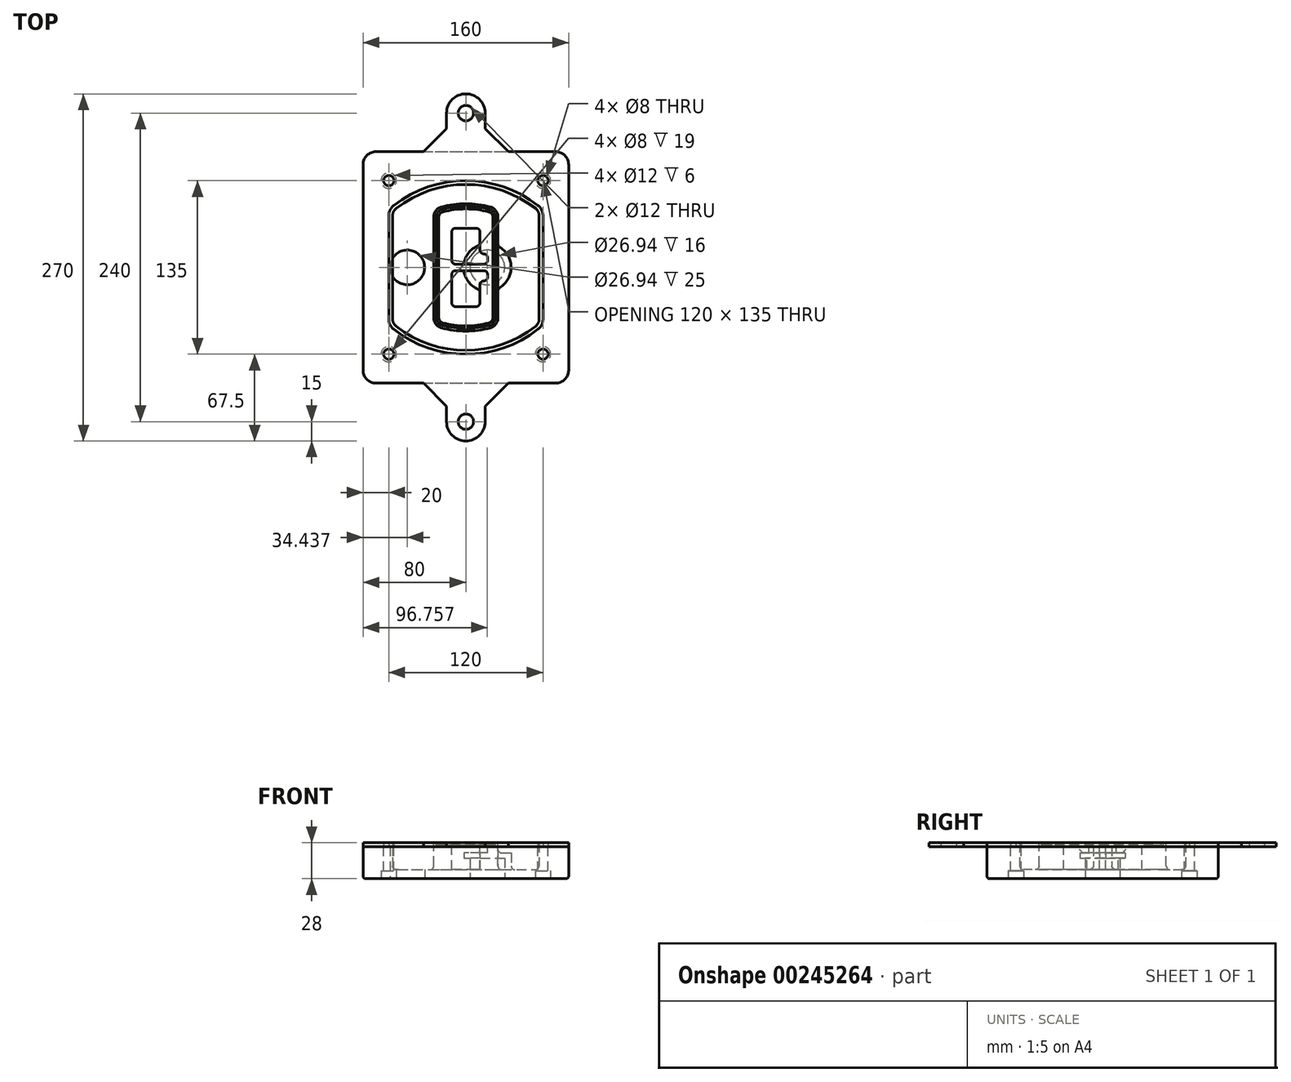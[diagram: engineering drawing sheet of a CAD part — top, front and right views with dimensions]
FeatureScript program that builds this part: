
annotation { "Feature Type Name" : "Feature", "Feature Type Description" : "" }
export const myFeature = defineFeature(function(context is Context, id is Id, definition is map)
    precondition{}
    {
        {
            var Q0;
            Q0=qCreatedBy(makeId("Top.planeOp"),FACE);
            var sketch = newSketch(context, id + "F0", { "sketchPlane" : qUnion([Q0])});
            skPoint(sketch, "E0.rect.middle", {"position": v(0, 0) * mm});
            skLineSegment(sketch, "E1.bottom", {"start": v(-70, -90) * mm, "end": v(70, -90) * mm});
            skLineSegment(sketch, "E1.top", {"start": v(-70, 90) * mm, "end": v(70, 90) * mm});
            skLineSegment(sketch, "E1.left", {"start": v(-80, -80) * mm, "end": v(-80, 80) * mm});
            skLineSegment(sketch, "E1.right", {"start": v(80, -80) * mm, "end": v(80, 80) * mm});
            skLineSegment(sketch, "E2", {"start": v(-80, 90) * mm, "end": v(80, -90) * mm, "construction": true});
            skLineSegment(sketch, "E3", {"start": v(80, 90) * mm, "end": v(-80, -90) * mm, "construction": true});
            skCircle(sketch, "E4", {"center": v(-60, 67.5) * mm, "radius": 4 * mm});
            skCircle(sketch, "E5", {"center": v(60, 67.5) * mm, "radius": 4 * mm});
            skCircle(sketch, "E6", {"center": v(60, -67.5) * mm, "radius": 4 * mm});
            skCircle(sketch, "E7", {"center": v(-60, -67.5) * mm, "radius": 4 * mm});
            skLineSegment(sketch, "E8", {"start": v(-60, 67.5) * mm, "end": v(60, 67.5) * mm, "construction": true});
            skLineSegment(sketch, "E9", {"start": v(60, 67.5) * mm, "end": v(60, -67.5) * mm, "construction": true});
            skLineSegment(sketch, "E10", {"start": v(60, -67.5) * mm, "end": v(-60, -67.5) * mm, "construction": true});
            skLineSegment(sketch, "E11", {"start": v(-60, -67.5) * mm, "end": v(-60, 67.5) * mm, "construction": true});
            skLineSegment(sketch, "E12", {"start": v(-60, 40.3) * mm, "end": v(-60, -40.3) * mm});
            skLineSegment(sketch, "E13", {"start": v(60, 40.3) * mm, "end": v(60, -40.3) * mm});
            skArc(sketch, "E14", {"start": v(56.15, 48.18) * mm, "mid": v(0, 67.5) * mm, "end": v(-56.15, 48.18) * mm});
            skArc(sketch, "E15", {"start": v(-56.15, -48.18) * mm, "mid": v(0, -67.5) * mm, "end": v(56.15, -48.18) * mm});
            skLineSegment(sketch, "E16", {"start": v(-60, 0) * mm, "end": v(60, 0) * mm, "construction": true});
            skPoint(sketch, "E17.visualSharp", {"position": v(-60, -45) * mm});
            skArc(sketch, "E17.filletArc", {"start": v(-60, -40.3) * mm, "mid": v(-58.99, -44.68) * mm, "end": v(-56.15, -48.18) * mm});
            skPoint(sketch, "E18.visualSharp", {"position": v(-60, 45) * mm});
            skArc(sketch, "E18.filletArc", {"start": v(-56.15, 48.18) * mm, "mid": v(-58.99, 44.68) * mm, "end": v(-60, 40.3) * mm});
            skPoint(sketch, "E19.visualSharp", {"position": v(60, 45) * mm});
            skArc(sketch, "E19.filletArc", {"start": v(60, 40.3) * mm, "mid": v(58.99, 44.68) * mm, "end": v(56.15, 48.18) * mm});
            skPoint(sketch, "E20.visualSharp", {"position": v(60, -45) * mm});
            skArc(sketch, "E20.filletArc", {"start": v(56.15, -48.18) * mm, "mid": v(58.99, -44.68) * mm, "end": v(60, -40.3) * mm});
            skPoint(sketch, "E21.visualSharp", {"position": v(-80, 90) * mm});
            skArc(sketch, "E21.filletArc", {"start": v(-70, 90) * mm, "mid": v(-77.07, 87.07) * mm, "end": v(-80, 80) * mm});
            skPoint(sketch, "E22.visualSharp", {"position": v(80, 90) * mm});
            skArc(sketch, "E22.filletArc", {"start": v(80, 80) * mm, "mid": v(77.07, 87.07) * mm, "end": v(70, 90) * mm});
            skPoint(sketch, "E23.visualSharp", {"position": v(80, -90) * mm});
            skArc(sketch, "E23.filletArc", {"start": v(70, -90) * mm, "mid": v(77.07, -87.07) * mm, "end": v(80, -80) * mm});
            skPoint(sketch, "E24.visualSharp", {"position": v(-80, -90) * mm});
            skArc(sketch, "E24.filletArc", {"start": v(-80, -80) * mm, "mid": v(-77.07, -87.07) * mm, "end": v(-70, -90) * mm});
            skArc(sketch, "E25.0", {"start": v(57, 40.3) * mm, "mid": v(56.3, 43.36) * mm, "end": v(54.3, 45.81) * mm});
            skLineSegment(sketch, "E25.1", {"start": v(57, 40.3) * mm, "end": v(57, -40.3) * mm});
            skArc(sketch, "E25.2", {"start": v(54.3, -45.81) * mm, "mid": v(56.3, -43.36) * mm, "end": v(57, -40.3) * mm});
            skArc(sketch, "E25.3", {"start": v(-54.3, -45.81) * mm, "mid": v(0, -64.5) * mm, "end": v(54.3, -45.81) * mm});
            skArc(sketch, "E25.4", {"start": v(-57, -40.3) * mm, "mid": v(-56.3, -43.36) * mm, "end": v(-54.3, -45.81) * mm});
            skArc(sketch, "E25.5", {"start": v(54.3, 45.81) * mm, "mid": v(0, 64.5) * mm, "end": v(-54.3, 45.81) * mm});
            skLineSegment(sketch, "E25.6", {"start": v(-57, 40.3) * mm, "end": v(-57, -40.3) * mm});
            skArc(sketch, "E25.7", {"start": v(-54.3, 45.81) * mm, "mid": v(-56.3, 43.36) * mm, "end": v(-57, 40.3) * mm});
            skArc(sketch, "E26.0", {"start": v(-58.62, 51.33) * mm, "mid": v(-62.58, 46.43) * mm, "end": v(-64, 40.3) * mm});
            skArc(sketch, "E26.1", {"start": v(58.62, 51.33) * mm, "mid": v(0, 71.5) * mm, "end": v(-58.62, 51.33) * mm});
            skArc(sketch, "E26.2", {"start": v(64, 40.3) * mm, "mid": v(62.58, 46.43) * mm, "end": v(58.62, 51.33) * mm});
            skLineSegment(sketch, "E26.3", {"start": v(64, 40.3) * mm, "end": v(64, -40.3) * mm});
            skArc(sketch, "E26.4", {"start": v(58.62, -51.33) * mm, "mid": v(62.58, -46.43) * mm, "end": v(64, -40.3) * mm});
            skLineSegment(sketch, "E26.5", {"start": v(-64, 40.3) * mm, "end": v(-64, -40.3) * mm});
            skArc(sketch, "E26.6", {"start": v(-58.62, -51.33) * mm, "mid": v(0, -71.5) * mm, "end": v(58.62, -51.33) * mm});
            skArc(sketch, "E26.7", {"start": v(-64, -40.3) * mm, "mid": v(-62.58, -46.43) * mm, "end": v(-58.62, -51.33) * mm});
            skSolve(sketch);
        }
        {
            var Q0;
            Q0=makeQuery(id+"F0.imprint","IMPRINT",FACE,{"disambiguationData":[TD([[makeQuery(id+"F0.imprint","IMPRINT",EDGE,{"derivedFrom":sQuery(id+"F0.wireOp",EDGE,"E1.bottom")}),1.0]])]});
            var Q1;
            Q1=makeQuery(id+"F0.imprint","IMPRINT",FACE,{"disambiguationData":[TD([[makeQuery(id+"F0.imprint","IMPRINT",EDGE,{"derivedFrom":sQuery(id+"F0.wireOp",EDGE,"E12")}),1.0]])]});
            var Q2;
            Q2=makeQuery(id+"F0.imprint","IMPRINT",FACE,{"disambiguationData":[TD([[makeQuery(id+"F0.imprint","IMPRINT",EDGE,{"derivedFrom":sQuery(id+"F0.wireOp",EDGE,"E25.0")}),1.0]])]});
            var Q3;
            Q3=makeQuery(id+"F0.imprint","IMPRINT",FACE,{"disambiguationData":[TD([[makeQuery(id+"F0.imprint","IMPRINT",EDGE,{"derivedFrom":sQuery(id+"F0.wireOp",EDGE,"E12")}),-1.0]])]});
            extrude(context, id + "F1", {"entities" : qUnion([Q0, Q1, Q2, Q3]), "oppositeDirection" : true, "depth" : 25 * mm});
        }
        {
            var Q0;
            Q0=makeQuery(id+"F0.imprint","IMPRINT",FACE,{"disambiguationData":[TD([[makeQuery(id+"F0.imprint","IMPRINT",EDGE,{"derivedFrom":sQuery(id+"F0.wireOp",EDGE,"E12")}),1.0]])]});
            extrude(context, id + "F2", {"entities" : qUnion([Q0]), "operationType" : NewBodyOperationType.ADD, "depth" : 3 * mm});
        }
        {
            var Q0;
            Q0=makeQuery(id+"F0.imprint","IMPRINT",FACE,{"disambiguationData":[TD([[makeQuery(id+"F0.imprint","IMPRINT",EDGE,{"derivedFrom":sQuery(id+"F0.wireOp",EDGE,"E25.0")}),1.0]])]});
            extrude(context, id + "F3", {"entities" : qUnion([Q0]), "operationType" : NewBodyOperationType.REMOVE, "oppositeDirection" : true, "depth" : 18 * mm});
        }
        {
            var Q0;
            Q0=makeQuery(id+"F2.opExtrude","CAP_FACE",FACE,{"disambiguationData":[OSD([sQuery(id+"F0.wireOp",EDGE,"E12"),sQuery(id+"F0.wireOp",EDGE,"E13"),sQuery(id+"F0.wireOp",EDGE,"E14"),sQuery(id+"F0.wireOp",EDGE,"E15"),sQuery(id+"F0.wireOp",EDGE,"E17.filletArc"),sQuery(id+"F0.wireOp",EDGE,"E18.filletArc"),sQuery(id+"F0.wireOp",EDGE,"E19.filletArc"),sQuery(id+"F0.wireOp",EDGE,"E20.filletArc"),sQuery(id+"F0.wireOp",EDGE,"E25.0"),sQuery(id+"F0.wireOp",EDGE,"E25.1"),sQuery(id+"F0.wireOp",EDGE,"E25.2"),sQuery(id+"F0.wireOp",EDGE,"E25.3"),sQuery(id+"F0.wireOp",EDGE,"E25.4"),sQuery(id+"F0.wireOp",EDGE,"E25.5"),sQuery(id+"F0.wireOp",EDGE,"E25.6"),sQuery(id+"F0.wireOp",EDGE,"E25.7")])],"isStart":false});
            var sketch = newSketch(context, id + "F4", { "sketchPlane" : qUnion([Q0])});
            skArc(sketch, "E27.0", {"start": v(-19.08, -46.97) * mm, "mid": v(0, -49.5) * mm, "end": v(19.08, -46.97) * mm});
            skArc(sketch, "E28.0", {"start": v(19.08, 46.97) * mm, "mid": v(0, 49.5) * mm, "end": v(-19.08, 46.97) * mm});
            skLineSegment(sketch, "E29", {"start": v(-25, 39.25) * mm, "end": v(-25, -39.25) * mm});
            skLineSegment(sketch, "E30", {"start": v(25, 39.25) * mm, "end": v(25, -39.25) * mm});
            skLineSegment(sketch, "E31", {"start": v(-25, 45.1) * mm, "end": v(25, 45.1) * mm, "construction": true});
            skLineSegment(sketch, "E32", {"start": v(-25, -45.1) * mm, "end": v(25, -45.1) * mm, "construction": true});
            skPoint(sketch, "E33.visualSharp", {"position": v(-25, 45.1) * mm});
            skArc(sketch, "E33.filletArc", {"start": v(-19.08, 46.97) * mm, "mid": v(-23.35, 44.11) * mm, "end": v(-25, 39.25) * mm});
            skPoint(sketch, "E34.visualSharp", {"position": v(25, 45.1) * mm});
            skArc(sketch, "E34.filletArc", {"start": v(25, 39.25) * mm, "mid": v(23.35, 44.11) * mm, "end": v(19.08, 46.97) * mm});
            skPoint(sketch, "E35.visualSharp", {"position": v(25, -45.1) * mm});
            skArc(sketch, "E35.filletArc", {"start": v(19.08, -46.97) * mm, "mid": v(23.35, -44.11) * mm, "end": v(25, -39.25) * mm});
            skPoint(sketch, "E36.visualSharp", {"position": v(-25, -45.1) * mm});
            skArc(sketch, "E36.filletArc", {"start": v(-25, -39.25) * mm, "mid": v(-23.35, -44.11) * mm, "end": v(-19.08, -46.97) * mm});
            skArc(sketch, "E37.0", {"start": v(54.3, 45.81) * mm, "mid": v(0, 64.5) * mm, "end": v(-54.3, 45.81) * mm});
            skArc(sketch, "E37.1", {"start": v(-54.3, 45.81) * mm, "mid": v(-56.3, 43.36) * mm, "end": v(-57, 40.3) * mm});
            skLineSegment(sketch, "E37.2", {"start": v(-57, 40.3) * mm, "end": v(-57, -40.3) * mm});
            skArc(sketch, "E37.3", {"start": v(-57, -40.3) * mm, "mid": v(-56.3, -43.36) * mm, "end": v(-54.3, -45.81) * mm});
            skArc(sketch, "E37.4", {"start": v(-54.3, -45.81) * mm, "mid": v(0, -64.5) * mm, "end": v(54.3, -45.81) * mm});
            skArc(sketch, "E37.5", {"start": v(54.3, -45.81) * mm, "mid": v(56.3, -43.36) * mm, "end": v(57, -40.3) * mm});
            skLineSegment(sketch, "E37.6", {"start": v(57, 40.3) * mm, "end": v(57, -40.3) * mm});
            skArc(sketch, "E37.7", {"start": v(57, 40.3) * mm, "mid": v(56.3, 43.36) * mm, "end": v(54.3, 45.81) * mm});
            skLineSegment(sketch, "E38.0", {"start": v(23, 39.25) * mm, "end": v(23, -39.25) * mm});
            skArc(sketch, "E38.1", {"start": v(18.56, -45.04) * mm, "mid": v(21.76, -42.9) * mm, "end": v(23, -39.25) * mm});
            skArc(sketch, "E38.2", {"start": v(-18.56, -45.04) * mm, "mid": v(0, -47.5) * mm, "end": v(18.56, -45.04) * mm});
            skArc(sketch, "E38.3", {"start": v(-23, -39.25) * mm, "mid": v(-21.76, -42.9) * mm, "end": v(-18.56, -45.04) * mm});
            skLineSegment(sketch, "E38.4", {"start": v(-23, 39.25) * mm, "end": v(-23, -39.25) * mm});
            skArc(sketch, "E38.5", {"start": v(23, 39.25) * mm, "mid": v(21.76, 42.9) * mm, "end": v(18.56, 45.04) * mm});
            skArc(sketch, "E38.6", {"start": v(-18.56, 45.04) * mm, "mid": v(-21.76, 42.9) * mm, "end": v(-23, 39.25) * mm});
            skArc(sketch, "E38.7", {"start": v(18.56, 45.04) * mm, "mid": v(0, 47.5) * mm, "end": v(-18.56, 45.04) * mm});
            skArc(sketch, "E39.0", {"start": v(21, 39.25) * mm, "mid": v(20.18, 41.68) * mm, "end": v(18.04, 43.1) * mm});
            skLineSegment(sketch, "E39.1", {"start": v(21, 39.25) * mm, "end": v(21, -39.25) * mm});
            skArc(sketch, "E39.2", {"start": v(18.04, -43.1) * mm, "mid": v(20.18, -41.68) * mm, "end": v(21, -39.25) * mm});
            skArc(sketch, "E39.3", {"start": v(-18.04, -43.1) * mm, "mid": v(0, -45.5) * mm, "end": v(18.04, -43.1) * mm});
            skArc(sketch, "E39.4", {"start": v(-21, -39.25) * mm, "mid": v(-20.18, -41.68) * mm, "end": v(-18.04, -43.1) * mm});
            skArc(sketch, "E39.5", {"start": v(18.04, 43.1) * mm, "mid": v(0, 45.5) * mm, "end": v(-18.04, 43.1) * mm});
            skLineSegment(sketch, "E39.6", {"start": v(-21, 39.25) * mm, "end": v(-21, -39.25) * mm});
            skArc(sketch, "E39.7", {"start": v(-18.04, 43.1) * mm, "mid": v(-20.18, 41.68) * mm, "end": v(-21, 39.25) * mm});
            skLineSegment(sketch, "E40", {"start": v(-25, 0) * mm, "end": v(25, 0) * mm, "construction": true});
            skLineSegment(sketch, "E41", {"start": v(-11, 5.5) * mm, "end": v(-11, 27.5) * mm});
            skLineSegment(sketch, "E42", {"start": v(-8, 30.5) * mm, "end": v(8, 30.5) * mm});
            skLineSegment(sketch, "E43", {"start": v(11, 27.5) * mm, "end": v(11, 13.5) * mm});
            skLineSegment(sketch, "E44", {"start": v(14, 10.5) * mm, "end": v(14, 10.5) * mm});
            skLineSegment(sketch, "E45", {"start": v(17, 7.5) * mm, "end": v(17, 5.5) * mm});
            skLineSegment(sketch, "E46", {"start": v(14, 2.5) * mm, "end": v(-8, 2.5) * mm});
            skPoint(sketch, "E47.visualSharp", {"position": v(-11, 30.5) * mm});
            skArc(sketch, "E47.filletArc", {"start": v(-8, 30.5) * mm, "mid": v(-10.12, 29.62) * mm, "end": v(-11, 27.5) * mm});
            skPoint(sketch, "E48.visualSharp", {"position": v(11, 30.5) * mm});
            skArc(sketch, "E48.filletArc", {"start": v(11, 27.5) * mm, "mid": v(10.12, 29.62) * mm, "end": v(8, 30.5) * mm});
            skPoint(sketch, "E49.visualSharp", {"position": v(11, 10.5) * mm});
            skArc(sketch, "E49.filletArc", {"start": v(11, 13.5) * mm, "mid": v(11.88, 11.38) * mm, "end": v(14, 10.5) * mm});
            skPoint(sketch, "E50.visualSharp", {"position": v(17, 10.5) * mm});
            skArc(sketch, "E50.filletArc", {"start": v(17, 7.5) * mm, "mid": v(16.12, 9.62) * mm, "end": v(14, 10.5) * mm});
            skPoint(sketch, "E51.visualSharp", {"position": v(17, 2.5) * mm});
            skArc(sketch, "E51.filletArc", {"start": v(14, 2.5) * mm, "mid": v(16.12, 3.38) * mm, "end": v(17, 5.5) * mm});
            skPoint(sketch, "E52.visualSharp", {"position": v(-11, 2.5) * mm});
            skArc(sketch, "E52.filletArc", {"start": v(-11, 5.5) * mm, "mid": v(-10.12, 3.38) * mm, "end": v(-8, 2.5) * mm});
            skLineSegment(sketch, "E53.0.MirrorCS", {"start": v(14, -2.5) * mm, "end": v(-8, -2.5) * mm});
            skArc(sketch, "E54.0.MirrorCS", {"start": v(-11, -5.5) * mm, "mid": v(-10.12, -3.38) * mm, "end": v(-8, -2.5) * mm});
            skLineSegment(sketch, "E55.0.MirrorCS", {"start": v(-11, -5.5) * mm, "end": v(-11, -27.5) * mm});
            skArc(sketch, "E56.0.MirrorCS", {"start": v(-8, -30.5) * mm, "mid": v(-10.12, -29.62) * mm, "end": v(-11, -27.5) * mm});
            skLineSegment(sketch, "E57.0.MirrorCS", {"start": v(-8, -30.5) * mm, "end": v(8, -30.5) * mm});
            skArc(sketch, "E58.0.MirrorCS", {"start": v(11, -27.5) * mm, "mid": v(10.12, -29.62) * mm, "end": v(8, -30.5) * mm});
            skLineSegment(sketch, "E59.0.MirrorCS", {"start": v(11, -27.5) * mm, "end": v(11, -13.5) * mm});
            skArc(sketch, "E60.0.MirrorCS", {"start": v(11, -13.5) * mm, "mid": v(11.88, -11.38) * mm, "end": v(14, -10.5) * mm});
            skArc(sketch, "E61.0.MirrorCS", {"start": v(17, -7.5) * mm, "mid": v(16.12, -9.62) * mm, "end": v(14, -10.5) * mm});
            skLineSegment(sketch, "E62.0.MirrorCS", {"start": v(17, -7.5) * mm, "end": v(17, -5.5) * mm});
            skArc(sketch, "E63.0.MirrorCS", {"start": v(14, -2.5) * mm, "mid": v(16.12, -3.38) * mm, "end": v(17, -5.5) * mm});
            skSolve(sketch);
        }
        {
            var Q0;
            Q0=makeQuery(id+"F4.imprint","IMPRINT",FACE,{"disambiguationData":[TD([[makeQuery(id+"F4.imprint","IMPRINT",EDGE,{"derivedFrom":sQuery(id+"F4.wireOp",EDGE,"E27.0")}),1.0]])]});
            var Q1;
            Q1=makeQuery(id+"F4.imprint","IMPRINT",FACE,{"disambiguationData":[TD([[makeQuery(id+"F4.imprint","IMPRINT",EDGE,{"derivedFrom":sQuery(id+"F4.wireOp",EDGE,"E38.0")}),-1.0]])]});
            var Q2;
            Q2=makeQuery(id+"F4.imprint","IMPRINT",FACE,{"disambiguationData":[TD([[makeQuery(id+"F4.imprint","IMPRINT",EDGE,{"derivedFrom":sQuery(id+"F4.wireOp",EDGE,"E39.0")}),1.0]])]});
            extrude(context, id + "F5", {"entities" : qUnion([Q0, Q1, Q2]), "operationType" : NewBodyOperationType.ADD, "endBound" : BoundingType.UP_TO_NEXT, "oppositeDirection" : true, "depth" : 25 * mm});
        }
        {
            var Q0;
            Q0=makeQuery(id+"F4.imprint","IMPRINT",FACE,{"disambiguationData":[TD([[makeQuery(id+"F4.imprint","IMPRINT",EDGE,{"derivedFrom":sQuery(id+"F4.wireOp",EDGE,"E38.0")}),-1.0]])]});
            extrude(context, id + "F6", {"entities" : qUnion([Q0]), "operationType" : NewBodyOperationType.REMOVE, "oppositeDirection" : true, "depth" : 2 * mm});
        }
        {
            var Q0;
            Q0=makeQuery(id+"F1.opExtrude","CAP_FACE",FACE,{"disambiguationData":[OSD([sQuery(id+"F0.wireOp",EDGE,"E1.bottom"),sQuery(id+"F0.wireOp",EDGE,"E1.top"),sQuery(id+"F0.wireOp",EDGE,"E1.left"),sQuery(id+"F0.wireOp",EDGE,"E1.right"),sQuery(id+"F0.wireOp",EDGE,"E4"),sQuery(id+"F0.wireOp",EDGE,"E5"),sQuery(id+"F0.wireOp",EDGE,"E6"),sQuery(id+"F0.wireOp",EDGE,"E7"),sQuery(id+"F0.wireOp",EDGE,"E21.filletArc"),sQuery(id+"F0.wireOp",EDGE,"E22.filletArc"),sQuery(id+"F0.wireOp",EDGE,"E23.filletArc"),sQuery(id+"F0.wireOp",EDGE,"E24.filletArc")])],"isStart":false});
            var sketch = newSketch(context, id + "F7", { "sketchPlane" : qUnion([Q0])});
            skCircle(sketch, "E64", {"center": v(16.76, 0) * mm, "radius": 13.47 * mm});
            skCircle(sketch, "E65", {"center": v(-45.56, 0) * mm, "radius": 13.47 * mm});
            skLineSegment(sketch, "E66", {"start": v(80, 0) * mm, "end": v(-80, 0) * mm});
            skCircle(sketch, "E67", {"center": v(16.76, 0) * mm, "radius": 18.47 * mm});
            skCircle(sketch, "E68", {"center": v(60, -67.5) * mm, "radius": 6 * mm});
            skCircle(sketch, "E69", {"center": v(-60, -67.5) * mm, "radius": 6 * mm});
            skCircle(sketch, "E70", {"center": v(-60, 67.5) * mm, "radius": 6 * mm});
            skCircle(sketch, "E71", {"center": v(60, 67.5) * mm, "radius": 6 * mm});
            skSolve(sketch);
        }
        {
            var Q0;
            {var subQ1=sQuery(id+"F7.wireOp",EDGE,"E66");var subQ4=sQuery(id+"F7.wireOp",EDGE,"E64");var subQ6=makeQuery(id+"F7.imprint","INTERSECT",VERTEX,{"disambiguationData":[OD(0.0)],"derivedFrom":[subQ4,subQ1]});Q0=makeQuery(id+"F7.imprint","IMPRINT",FACE,{"disambiguationData":[TD([[makeQuery(id+"F7.imprint","IMPRINT",EDGE,{"disambiguationData":[TD([[subQ6,-1.0]])],"derivedFrom":subQ4}),-1.0]])]});}
            var Q1;
            {var subQ0=sQuery(id+"F7.wireOp",EDGE,"E66");var subQ1=sQuery(id+"F7.wireOp",EDGE,"E64");var subQ3=makeQuery(id+"F7.imprint","INTERSECT",VERTEX,{"disambiguationData":[OD(0.0)],"derivedFrom":[subQ1,subQ0]});Q1=makeQuery(id+"F7.imprint","IMPRINT",FACE,{"disambiguationData":[TD([[makeQuery(id+"F7.imprint","IMPRINT",EDGE,{"disambiguationData":[TD([[subQ3,-1.0]])],"derivedFrom":subQ1}),1.0]])]});}
            var Q2;
            {var subQ0=sQuery(id+"F7.wireOp",EDGE,"E66");var subQ1=sQuery(id+"F7.wireOp",EDGE,"E64");var subQ3=makeQuery(id+"F7.imprint","INTERSECT",VERTEX,{"disambiguationData":[OD(0.0)],"derivedFrom":[subQ1,subQ0]});Q2=makeQuery(id+"F7.imprint","IMPRINT",FACE,{"disambiguationData":[TD([[makeQuery(id+"F7.imprint","IMPRINT",EDGE,{"disambiguationData":[TD([[subQ3,1.0]])],"derivedFrom":subQ1}),1.0]])]});}
            var Q3;
            {var subQ1=sQuery(id+"F7.wireOp",EDGE,"E66");var subQ4=sQuery(id+"F7.wireOp",EDGE,"E64");var subQ6=makeQuery(id+"F7.imprint","INTERSECT",VERTEX,{"disambiguationData":[OD(0.0)],"derivedFrom":[subQ4,subQ1]});Q3=makeQuery(id+"F7.imprint","IMPRINT",FACE,{"disambiguationData":[TD([[makeQuery(id+"F7.imprint","IMPRINT",EDGE,{"disambiguationData":[TD([[subQ6,1.0]])],"derivedFrom":subQ4}),-1.0]])]});}
            extrude(context, id + "F8", {"entities" : qUnion([Q0, Q1, Q2, Q3]), "operationType" : NewBodyOperationType.ADD, "oppositeDirection" : true, "depth" : 20 * mm});
        }
        {
            var Q0;
            {var subQ0=sQuery(id+"F7.wireOp",EDGE,"E66");var subQ1=sQuery(id+"F7.wireOp",EDGE,"E64");var subQ3=makeQuery(id+"F7.imprint","INTERSECT",VERTEX,{"disambiguationData":[OD(0.0)],"derivedFrom":[subQ1,subQ0]});Q0=makeQuery(id+"F7.imprint","IMPRINT",FACE,{"disambiguationData":[TD([[makeQuery(id+"F7.imprint","IMPRINT",EDGE,{"disambiguationData":[TD([[subQ3,-1.0]])],"derivedFrom":subQ1}),1.0]])]});}
            var Q1;
            {var subQ0=sQuery(id+"F7.wireOp",EDGE,"E66");var subQ1=sQuery(id+"F7.wireOp",EDGE,"E64");var subQ3=makeQuery(id+"F7.imprint","INTERSECT",VERTEX,{"disambiguationData":[OD(0.0)],"derivedFrom":[subQ1,subQ0]});Q1=makeQuery(id+"F7.imprint","IMPRINT",FACE,{"disambiguationData":[TD([[makeQuery(id+"F7.imprint","IMPRINT",EDGE,{"disambiguationData":[TD([[subQ3,1.0]])],"derivedFrom":subQ1}),1.0]])]});}
            extrude(context, id + "F9", {"entities" : qUnion([Q0, Q1]), "operationType" : NewBodyOperationType.REMOVE, "oppositeDirection" : true, "depth" : 16 * mm});
        }
        {
            var Q0;
            {var subQ0=sQuery(id+"F7.wireOp",EDGE,"E66");var subQ1=sQuery(id+"F7.wireOp",EDGE,"E65");var subQ3=makeQuery(id+"F7.imprint","INTERSECT",VERTEX,{"disambiguationData":[OD(0.0)],"derivedFrom":[subQ1,subQ0]});Q0=makeQuery(id+"F7.imprint","IMPRINT",FACE,{"disambiguationData":[TD([[makeQuery(id+"F7.imprint","IMPRINT",EDGE,{"disambiguationData":[TD([[subQ3,-1.0]])],"derivedFrom":subQ1}),1.0]])]});}
            var Q1;
            {var subQ0=sQuery(id+"F7.wireOp",EDGE,"E66");var subQ1=sQuery(id+"F7.wireOp",EDGE,"E65");var subQ3=makeQuery(id+"F7.imprint","INTERSECT",VERTEX,{"disambiguationData":[OD(0.0)],"derivedFrom":[subQ1,subQ0]});Q1=makeQuery(id+"F7.imprint","IMPRINT",FACE,{"disambiguationData":[TD([[makeQuery(id+"F7.imprint","IMPRINT",EDGE,{"disambiguationData":[TD([[subQ3,1.0]])],"derivedFrom":subQ1}),1.0]])]});}
            extrude(context, id + "F10", {"entities" : qUnion([Q0, Q1]), "operationType" : NewBodyOperationType.REMOVE, "oppositeDirection" : true, "depth" : 25 * mm});
        }
        {
            var Q0;
            Q0=makeQuery(id+"F7.imprint","IMPRINT",FACE,{"disambiguationData":[TD([[makeQuery(id+"F7.imprint","IMPRINT",EDGE,{"derivedFrom":sQuery(id+"F7.wireOp",EDGE,"E68")}),1.0]])]});
            var Q1;
            Q1=makeQuery(id+"F7.imprint","IMPRINT",FACE,{"disambiguationData":[TD([[makeQuery(id+"F7.imprint","IMPRINT",EDGE,{"derivedFrom":makeQuery(id+"F1.opExtrude","CAP_EDGE",EDGE,{"disambiguationData":[OSD([sQuery(id+"F0.wireOp",EDGE,"E5")])],"isStart":false})}),-1.0]])]});
            var Q2;
            Q2=makeQuery(id+"F7.imprint","IMPRINT",FACE,{"disambiguationData":[TD([[makeQuery(id+"F7.imprint","IMPRINT",EDGE,{"derivedFrom":sQuery(id+"F7.wireOp",EDGE,"E69")}),1.0]])]});
            var Q3;
            Q3=makeQuery(id+"F7.imprint","IMPRINT",FACE,{"disambiguationData":[TD([[makeQuery(id+"F7.imprint","IMPRINT",EDGE,{"derivedFrom":makeQuery(id+"F1.opExtrude","CAP_EDGE",EDGE,{"disambiguationData":[OSD([sQuery(id+"F0.wireOp",EDGE,"E4")])],"isStart":false})}),-1.0]])]});
            var Q4;
            Q4=makeQuery(id+"F7.imprint","IMPRINT",FACE,{"disambiguationData":[TD([[makeQuery(id+"F7.imprint","IMPRINT",EDGE,{"derivedFrom":sQuery(id+"F7.wireOp",EDGE,"E70")}),1.0]])]});
            var Q5;
            Q5=makeQuery(id+"F7.imprint","IMPRINT",FACE,{"disambiguationData":[TD([[makeQuery(id+"F7.imprint","IMPRINT",EDGE,{"derivedFrom":makeQuery(id+"F1.opExtrude","CAP_EDGE",EDGE,{"disambiguationData":[OSD([sQuery(id+"F0.wireOp",EDGE,"E7")])],"isStart":false})}),-1.0]])]});
            var Q6;
            Q6=makeQuery(id+"F7.imprint","IMPRINT",FACE,{"disambiguationData":[TD([[makeQuery(id+"F7.imprint","IMPRINT",EDGE,{"derivedFrom":sQuery(id+"F7.wireOp",EDGE,"E71")}),1.0]])]});
            var Q7;
            Q7=makeQuery(id+"F7.imprint","IMPRINT",FACE,{"disambiguationData":[TD([[makeQuery(id+"F7.imprint","IMPRINT",EDGE,{"derivedFrom":makeQuery(id+"F1.opExtrude","CAP_EDGE",EDGE,{"disambiguationData":[OSD([sQuery(id+"F0.wireOp",EDGE,"E6")])],"isStart":false})}),-1.0]])]});
            extrude(context, id + "F11", {"entities" : qUnion([Q0, Q1, Q2, Q3, Q4, Q5, Q6, Q7]), "operationType" : NewBodyOperationType.REMOVE, "oppositeDirection" : true, "depth" : 6 * mm});
        }
        {
            var Q0;
            Q0=makeQuery(id+"F9.boolean.opBoolean","COPY",FACE,{"derivedFrom":makeQuery(id+"F9.opExtrude","CAP_FACE",FACE,{"disambiguationData":[OSD([sQuery(id+"F7.wireOp",EDGE,"E64")])],"isStart":false})});
            var sketch = newSketch(context, id + "F12", { "sketchPlane" : qUnion([Q0])});
            skArc(sketch, "E72.0", {"start": v(11, 17.55) * mm, "mid": v(2.57, 11.82) * mm, "end": v(-1.54, 2.5) * mm});
            skArc(sketch, "E72.1", {"start": v(-1.54, -2.5) * mm, "mid": v(2.57, -11.82) * mm, "end": v(11, -17.55) * mm});
            skLineSegment(sketch, "E73", {"start": v(-1.54, -2.5) * mm, "end": v(14, -2.5) * mm});
            skLineSegment(sketch, "E74.0", {"start": v(14, 2.5) * mm, "end": v(-1.54, 2.5) * mm});
            skArc(sketch, "E74.1", {"start": v(14, 2.5) * mm, "mid": v(16.12, 3.38) * mm, "end": v(17, 5.5) * mm});
            skLineSegment(sketch, "E74.2", {"start": v(17, 7.5) * mm, "end": v(17, 5.5) * mm});
            skArc(sketch, "E74.3", {"start": v(17, 7.5) * mm, "mid": v(16.12, 9.62) * mm, "end": v(14, 10.5) * mm});
            skArc(sketch, "E74.4", {"start": v(11, 13.5) * mm, "mid": v(11.88, 11.38) * mm, "end": v(14, 10.5) * mm});
            skLineSegment(sketch, "E74.5", {"start": v(11, 17.55) * mm, "end": v(11, 13.5) * mm});
            skLineSegment(sketch, "E74.7", {"start": v(14, -2.5) * mm, "end": v(-1.54, -2.5) * mm});
            skArc(sketch, "E74.8", {"start": v(14, -2.5) * mm, "mid": v(16.12, -3.38) * mm, "end": v(17, -5.5) * mm});
            skLineSegment(sketch, "E74.9", {"start": v(17, -7.5) * mm, "end": v(17, -5.5) * mm});
            skArc(sketch, "E74.10", {"start": v(17, -7.5) * mm, "mid": v(16.12, -9.62) * mm, "end": v(14, -10.5) * mm});
            skArc(sketch, "E74.11", {"start": v(11, -13.5) * mm, "mid": v(11.88, -11.38) * mm, "end": v(14, -10.5) * mm});
            skLineSegment(sketch, "E74.12", {"start": v(11, -17.55) * mm, "end": v(11, -13.5) * mm});
            skPoint(sketch, "E75.orphan", {"position": v(11, -27.5) * mm});
            skPoint(sketch, "E76.orphan", {"position": v(-8, -2.5) * mm});
            skPoint(sketch, "E77.orphan", {"position": v(-8, 2.5) * mm});
            skPoint(sketch, "E78.orphan", {"position": v(11, 27.5) * mm});
            skSolve(sketch);
        }
        {
            var Q0;
            {var subQ7=sQuery(id+"F12.wireOp",EDGE,"E72.0");var subQ14=sQuery(id+"F12.wireOp",EDGE,"E72.1");var subQ16=sQuery(id+"F12.wireOp",EDGE,"E74.1");var subQ18=sQuery(id+"F12.wireOp",EDGE,"E74.8");Q0=qUnion([makeQuery(id+"F12.imprint","IMPRINT",FACE,{"disambiguationData":[TD([[makeQuery(id+"F12.imprint","IMPRINT",EDGE,{"derivedFrom":subQ7}),1.0]])]}),makeQuery(id+"F12.imprint","IMPRINT",FACE,{"disambiguationData":[TD([[makeQuery(id+"F12.imprint","IMPRINT",EDGE,{"derivedFrom":subQ14}),1.0]])]}),makeQuery(id+"F12.imprint","IMPRINT",FACE,{"disambiguationData":[TD([[makeQuery(id+"F12.imprint","IMPRINT",EDGE,{"derivedFrom":subQ16}),1.0]])]}),makeQuery(id+"F12.imprint","IMPRINT",FACE,{"disambiguationData":[TD([[makeQuery(id+"F12.imprint","IMPRINT",EDGE,{"derivedFrom":subQ18}),-1.0]])]})]);}
            var Q1;
            Q1=makeQuery(id+"F5.boolean.opBoolean","SPLIT",FACE,{"disambiguationData":[TD([makeQuery(id+"F5.opExtrude","SWEPT_FACE",FACE,{"disambiguationData":[OSD([sQuery(id+"F4.wireOp",EDGE,"E41")])]})])],"derivedFrom":makeQuery(id+"F3.boolean.opBoolean","COPY",FACE,{"derivedFrom":makeQuery(id+"F3.opExtrude","CAP_FACE",FACE,{"disambiguationData":[OSD([sQuery(id+"F0.wireOp",EDGE,"E25.0"),sQuery(id+"F0.wireOp",EDGE,"E25.1"),sQuery(id+"F0.wireOp",EDGE,"E25.2"),sQuery(id+"F0.wireOp",EDGE,"E25.3"),sQuery(id+"F0.wireOp",EDGE,"E25.4"),sQuery(id+"F0.wireOp",EDGE,"E25.5"),sQuery(id+"F0.wireOp",EDGE,"E25.6"),sQuery(id+"F0.wireOp",EDGE,"E25.7")])],"isStart":false})})});
            extrude(context, id + "F13", {"entities" : qUnion([Q0]), "operationType" : NewBodyOperationType.REMOVE, "endBound" : BoundingType.UP_TO_SURFACE, "endBoundEntityFace" : qUnion([Q1]), "depth" : 25 * mm});
        }
        {
            var Q0;
            Q0=makeQuery(id+"F3.boolean.opBoolean","COPY",EDGE,{"derivedFrom":makeQuery(id+"F3.opExtrude","CAP_EDGE",EDGE,{"disambiguationData":[OSD([sQuery(id+"F0.wireOp",EDGE,"E25.6")])],"isStart":false})});
            var Q1;
            Q1=makeQuery(id+"F8.boolean.opBoolean","INTERSECT",EDGE,{"derivedFrom":[makeQuery(id+"F5.opExtrude","SWEPT_FACE",FACE,{"disambiguationData":[OSD([sQuery(id+"F4.wireOp",EDGE,"E30")])]}),makeQuery(id+"F8.opExtrude","CAP_FACE",FACE,{"disambiguationData":[OSD([sQuery(id+"F7.wireOp",EDGE,"E67")])],"isStart":false})]});
            var Q2;
            Q2=makeQuery(id+"F8.boolean.opBoolean","INTERSECT",EDGE,{"disambiguationData":[OD(1.0)],"derivedFrom":[makeQuery(id+"F5.opExtrude","SWEPT_FACE",FACE,{"disambiguationData":[OSD([sQuery(id+"F4.wireOp",EDGE,"E30")])]}),makeQuery(id+"F8.opExtrude","SWEPT_FACE",FACE,{"disambiguationData":[OSD([sQuery(id+"F7.wireOp",EDGE,"E67")])]})]});
            var Q3;
            {var subQ0=sQuery(id+"F4.wireOp",EDGE,"E30");Q3=makeQuery(id+"F8.boolean.opBoolean","SPLIT",EDGE,{"disambiguationData":[TD([makeQuery(id+"F5.opExtrude","SWEPT_FACE",FACE,{"disambiguationData":[OSD([sQuery(id+"F4.wireOp",EDGE,"E35.filletArc")])]})])],"derivedFrom":makeQuery(id+"F5.opExtrude","CAP_EDGE",EDGE,{"disambiguationData":[OSD([subQ0])],"isStart":false})});}
            var Q4;
            {var subQ0=sQuery(id+"F0.wireOp",EDGE,"E25.7");var subQ1=sQuery(id+"F0.wireOp",EDGE,"E25.1");var subQ2=sQuery(id+"F0.wireOp",EDGE,"E25.6");var subQ3=sQuery(id+"F0.wireOp",EDGE,"E25.5");var subQ4=sQuery(id+"F0.wireOp",EDGE,"E25.4");var subQ5=sQuery(id+"F0.wireOp",EDGE,"E25.0");var subQ6=sQuery(id+"F0.wireOp",EDGE,"E25.2");var subQ7=sQuery(id+"F0.wireOp",EDGE,"E25.3");Q4=makeQuery(id+"F8.boolean.opBoolean","INTERSECT",EDGE,{"derivedFrom":[makeQuery(id+"F5.boolean.opBoolean","SPLIT",FACE,{"disambiguationData":[TD([makeQuery(id+"F2.opExtrude","SWEPT_FACE",FACE,{"disambiguationData":[OSD([subQ5])]})])],"derivedFrom":makeQuery(id+"F3.boolean.opBoolean","COPY",FACE,{"derivedFrom":makeQuery(id+"F3.opExtrude","CAP_FACE",FACE,{"disambiguationData":[OSD([subQ5,subQ1,subQ6,subQ7,subQ4,subQ3,subQ2,subQ0])],"isStart":false})})}),makeQuery(id+"F8.opExtrude","SWEPT_FACE",FACE,{"disambiguationData":[OSD([sQuery(id+"F7.wireOp",EDGE,"E67")])]})]});}
            var Q5;
            Q5=makeQuery(id+"F8.boolean.opBoolean","INTERSECT",EDGE,{"disambiguationData":[OD(0.0)],"derivedFrom":[makeQuery(id+"F5.opExtrude","SWEPT_FACE",FACE,{"disambiguationData":[OSD([sQuery(id+"F4.wireOp",EDGE,"E30")])]}),makeQuery(id+"F8.opExtrude","SWEPT_FACE",FACE,{"disambiguationData":[OSD([sQuery(id+"F7.wireOp",EDGE,"E67")])]})]});
            fillet(context, id + "F14", {"entities" : qUnion([Q0, Q1, Q2, Q3, Q4, Q5]), "radius" : 3 * mm, "tangentPropagation" : true, "allowEdgeOverflow" : false});
        }
        {
            var Q0;
            Q0=makeQuery(id+"F1.opExtrude","CAP_EDGE",EDGE,{"disambiguationData":[OSD([sQuery(id+"F0.wireOp",EDGE,"E1.bottom")])],"isStart":false});
            fillet(context, id + "F15", {"entities" : qUnion([Q0]), "radius" : 2 * mm, "tangentPropagation" : true, "allowEdgeOverflow" : false});
        }
        {
            var Q0;
            {var subQ0=sQuery(id+"F0.wireOp",EDGE,"E22.filletArc");var subQ1=sQuery(id+"F0.wireOp",EDGE,"E7");var subQ2=sQuery(id+"F0.wireOp",EDGE,"E6");var subQ3=sQuery(id+"F0.wireOp",EDGE,"E5");var subQ4=sQuery(id+"F0.wireOp",EDGE,"E4");var subQ5=sQuery(id+"F0.wireOp",EDGE,"E1.bottom");var subQ6=sQuery(id+"F0.wireOp",EDGE,"E21.filletArc");var subQ7=sQuery(id+"F0.wireOp",EDGE,"E1.top");var subQ8=sQuery(id+"F0.wireOp",EDGE,"E1.left");var subQ9=sQuery(id+"F0.wireOp",EDGE,"E1.right");var subQ10=sQuery(id+"F0.wireOp",EDGE,"E23.filletArc");var subQ11=sQuery(id+"F0.wireOp",EDGE,"E24.filletArc");Q0=makeQuery(id+"F2.boolean.opBoolean","SPLIT",FACE,{"disambiguationData":[TD([makeQuery(id+"F1.opExtrude","SWEPT_FACE",FACE,{"disambiguationData":[OSD([subQ5])]})])],"derivedFrom":makeQuery(id+"F1.opExtrude","CAP_FACE",FACE,{"disambiguationData":[OSD([subQ5,subQ7,subQ8,subQ9,subQ4,subQ3,subQ2,subQ1,subQ6,subQ0,subQ10,subQ11])],"isStart":true})});}
            var sketch = newSketch(context, id + "F16", { "sketchPlane" : qUnion([Q0])});
            skLineSegment(sketch, "E79.0", {"start": v(-80, -80) * mm, "end": v(-80, 80) * mm});
            skArc(sketch, "E79.1", {"start": v(-70, 90) * mm, "mid": v(-77.07, 87.07) * mm, "end": v(-80, 80) * mm});
            skLineSegment(sketch, "E79.2", {"start": v(-70, 90) * mm, "end": v(70, 90) * mm});
            skArc(sketch, "E79.3", {"start": v(80, 80) * mm, "mid": v(77.07, 87.07) * mm, "end": v(70, 90) * mm});
            skLineSegment(sketch, "E79.4", {"start": v(80, -80) * mm, "end": v(80, 80) * mm});
            skArc(sketch, "E79.5", {"start": v(70, -90) * mm, "mid": v(77.07, -87.07) * mm, "end": v(80, -80) * mm});
            skLineSegment(sketch, "E79.6", {"start": v(-70, -90) * mm, "end": v(70, -90) * mm});
            skArc(sketch, "E79.7", {"start": v(-80, -80) * mm, "mid": v(-77.07, -87.07) * mm, "end": v(-70, -90) * mm});
            skCircle(sketch, "E79.8", {"center": v(-60, -67.5) * mm, "radius": 4 * mm});
            skCircle(sketch, "E79.9", {"center": v(-60, 67.5) * mm, "radius": 4 * mm});
            skCircle(sketch, "E79.10", {"center": v(60, 67.5) * mm, "radius": 4 * mm});
            skCircle(sketch, "E79.11", {"center": v(60, -67.5) * mm, "radius": 4 * mm});
            skArc(sketch, "E79.12", {"start": v(-56.15, -48.18) * mm, "mid": v(0, -67.5) * mm, "end": v(56.15, -48.18) * mm});
            skArc(sketch, "E79.13", {"start": v(56.15, -48.18) * mm, "mid": v(58.99, -44.68) * mm, "end": v(60, -40.3) * mm});
            skLineSegment(sketch, "E79.14", {"start": v(60, 40.3) * mm, "end": v(60, -40.3) * mm});
            skArc(sketch, "E79.15", {"start": v(60, 40.3) * mm, "mid": v(58.99, 44.68) * mm, "end": v(56.15, 48.18) * mm});
            skArc(sketch, "E79.16", {"start": v(56.15, 48.18) * mm, "mid": v(0, 67.5) * mm, "end": v(-56.15, 48.18) * mm});
            skArc(sketch, "E79.17", {"start": v(-56.15, 48.18) * mm, "mid": v(-58.99, 44.68) * mm, "end": v(-60, 40.3) * mm});
            skLineSegment(sketch, "E79.18", {"start": v(-60, 40.3) * mm, "end": v(-60, -40.3) * mm});
            skArc(sketch, "E79.19", {"start": v(-60, -40.3) * mm, "mid": v(-58.99, -44.68) * mm, "end": v(-56.15, -48.18) * mm});
            skLineSegment(sketch, "E80", {"start": v(0, 90) * mm, "end": v(0, 120) * mm, "construction": true});
            skPoint(sketch, "E80.endSnap0", {"position": v(0, 90) * mm});
            skCircle(sketch, "E81", {"center": v(0, 120) * mm, "radius": 6 * mm});
            skArc(sketch, "E82", {"start": v(15, 120) * mm, "mid": v(0, 135) * mm, "end": v(-15, 120) * mm});
            skLineSegment(sketch, "E83", {"start": v(-15, 120) * mm, "end": v(-15, 108) * mm});
            skLineSegment(sketch, "E84", {"start": v(-15, 108) * mm, "end": v(-33, 90) * mm});
            skLineSegment(sketch, "E85.MirrorCS", {"start": v(15, 120) * mm, "end": v(15, 108) * mm});
            skLineSegment(sketch, "E86.MirrorCS", {"start": v(15, 108) * mm, "end": v(33, 90) * mm});
            skLineSegment(sketch, "E87", {"start": v(-80, 0) * mm, "end": v(80, 0) * mm, "construction": true});
            skArc(sketch, "E88.MirrorCS", {"start": v(-15, 120) * mm, "mid": v(0, 135) * mm, "end": v(15, 120) * mm});
            skArc(sketch, "E89.MirrorCS", {"start": v(15, -120) * mm, "mid": v(0, -135) * mm, "end": v(-15, -120) * mm});
            skCircle(sketch, "E90.MirrorC", {"center": v(0, -120) * mm, "radius": 6 * mm});
            skLineSegment(sketch, "E91.MirrorCS", {"start": v(15, -120) * mm, "end": v(15, -108) * mm});
            skLineSegment(sketch, "E92.MirrorCS", {"start": v(15, -108) * mm, "end": v(33, -90) * mm});
            skLineSegment(sketch, "E93.MirrorCS", {"start": v(-15, -120) * mm, "end": v(-15, -108) * mm});
            skLineSegment(sketch, "E94.MirrorCS", {"start": v(-15, -108) * mm, "end": v(-33, -90) * mm});
            skLineSegment(sketch, "E95.MirrorCS", {"start": v(0, -90) * mm, "end": v(0, -120) * mm, "construction": true});
            skSolve(sketch);
        }
        {
            var Q0;
            Q0 = qSketchRegion(id + "F16", true);
            var Q1;
            Q1=makeQuery(id+"F2.opExtrude","CAP_FACE",FACE,{"disambiguationData":[OSD([sQuery(id+"F0.wireOp",EDGE,"E12"),sQuery(id+"F0.wireOp",EDGE,"E13"),sQuery(id+"F0.wireOp",EDGE,"E14"),sQuery(id+"F0.wireOp",EDGE,"E15"),sQuery(id+"F0.wireOp",EDGE,"E17.filletArc"),sQuery(id+"F0.wireOp",EDGE,"E18.filletArc"),sQuery(id+"F0.wireOp",EDGE,"E19.filletArc"),sQuery(id+"F0.wireOp",EDGE,"E20.filletArc"),sQuery(id+"F0.wireOp",EDGE,"E25.0"),sQuery(id+"F0.wireOp",EDGE,"E25.1"),sQuery(id+"F0.wireOp",EDGE,"E25.2"),sQuery(id+"F0.wireOp",EDGE,"E25.3"),sQuery(id+"F0.wireOp",EDGE,"E25.4"),sQuery(id+"F0.wireOp",EDGE,"E25.5"),sQuery(id+"F0.wireOp",EDGE,"E25.6"),sQuery(id+"F0.wireOp",EDGE,"E25.7")])],"isStart":false});
            extrude(context, id + "F17", {"entities" : qUnion([Q0]), "endBound" : BoundingType.UP_TO_SURFACE, "endBoundEntityFace" : qUnion([Q1]), "depth" : 25 * mm});
        }
    });
